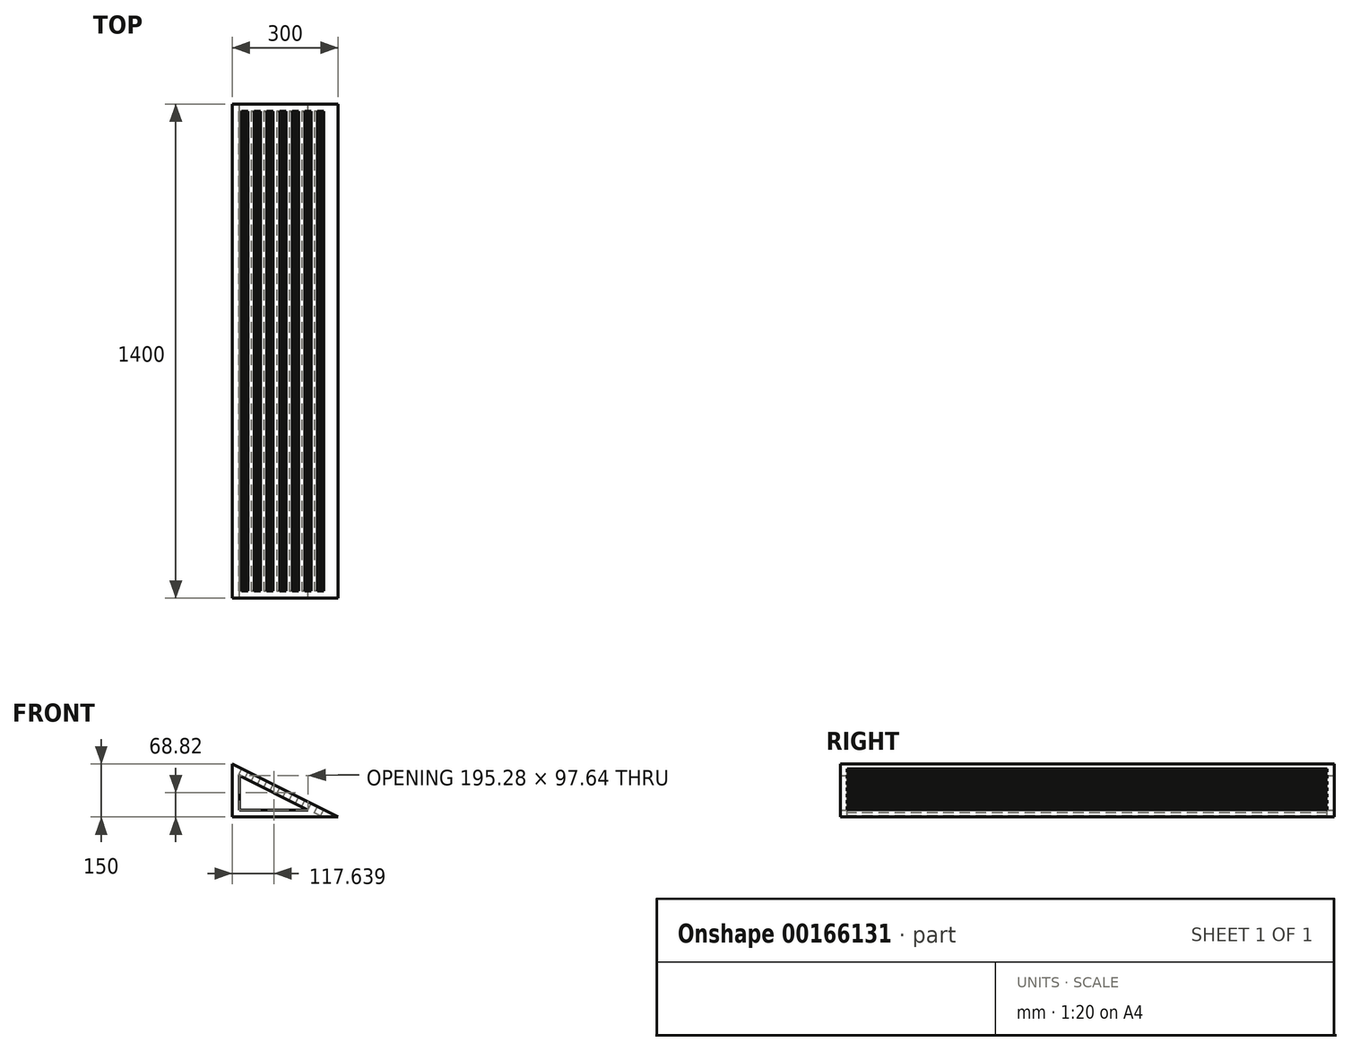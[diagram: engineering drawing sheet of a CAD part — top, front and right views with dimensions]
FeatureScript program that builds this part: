
annotation { "Feature Type Name" : "Feature", "Feature Type Description" : "" }
export const myFeature = defineFeature(function(context is Context, id is Id, definition is map)
    precondition{}
    {
        {
            var Q0;
            Q0=qCreatedBy(makeId("Front.planeOp"),FACE);
            var sketch = newSketch(context, id + "F0", { "sketchPlane" : qUnion([Q0])});
            skLineSegment(sketch, "E0", {"start": v(0, 0) * mm, "end": v(0, 150) * mm});
            skLineSegment(sketch, "E1", {"start": v(0, 150) * mm, "end": v(300, 0) * mm});
            skLineSegment(sketch, "E2", {"start": v(300, 0) * mm, "end": v(0, 0) * mm});
            skLineSegment(sketch, "E3", {"start": v(20, 20) * mm, "end": v(20, 117.64) * mm});
            skLineSegment(sketch, "E4", {"start": v(20, 117.64) * mm, "end": v(215.28, 20) * mm});
            skLineSegment(sketch, "E5", {"start": v(215.28, 20) * mm, "end": v(20, 20) * mm});
            skSolve(sketch);
        }
        {
            var Q0;
            Q0 = qSketchRegion(id + "F0", true);
            extrude(context, id + "F1", {"entities" : qUnion([Q0]), "depth" : 1400 * mm});
        }
        {
            var Q0;
            Q0=makeQuery(id+"F1.opExtrude","SWEPT_FACE",FACE,{"disambiguationData":[OSD([sQuery(id+"F0.wireOp",EDGE,"E1")])]});
            var sketch = newSketch(context, id + "F2", { "sketchPlane" : qUnion([Q0])});
            skLineSegment(sketch, "E6.bottom", {"start": v(-37.08, -1380) * mm, "end": v(-17.08, -1380) * mm});
            skLineSegment(sketch, "E6.top", {"start": v(-37.08, -20) * mm, "end": v(-17.08, -20) * mm});
            skLineSegment(sketch, "E6.left", {"start": v(-37.08, -1380) * mm, "end": v(-37.08, -20) * mm});
            skLineSegment(sketch, "E6.right", {"start": v(-17.08, -1380) * mm, "end": v(-17.08, -20) * mm});
            skLineSegment(sketch, "E7.bottom", {"start": v(2.92, -1380) * mm, "end": v(22.92, -1380) * mm});
            skLineSegment(sketch, "E7.top", {"start": v(2.92, -20) * mm, "end": v(22.92, -20) * mm});
            skLineSegment(sketch, "E7.left", {"start": v(2.92, -1380) * mm, "end": v(2.92, -20) * mm});
            skLineSegment(sketch, "E7.right", {"start": v(22.92, -1380) * mm, "end": v(22.92, -20) * mm});
            skLineSegment(sketch, "E8.bottom", {"start": v(42.92, -1380) * mm, "end": v(62.92, -1380) * mm});
            skLineSegment(sketch, "E8.top", {"start": v(42.92, -20) * mm, "end": v(62.92, -20) * mm});
            skLineSegment(sketch, "E8.left", {"start": v(42.92, -1380) * mm, "end": v(42.92, -20) * mm});
            skLineSegment(sketch, "E8.right", {"start": v(62.92, -1380) * mm, "end": v(62.92, -20) * mm});
            skLineSegment(sketch, "E9.bottom", {"start": v(82.92, -1380) * mm, "end": v(102.92, -1380) * mm});
            skLineSegment(sketch, "E9.top", {"start": v(82.92, -20) * mm, "end": v(102.92, -20) * mm});
            skLineSegment(sketch, "E9.left", {"start": v(82.92, -1380) * mm, "end": v(82.92, -20) * mm});
            skLineSegment(sketch, "E9.right", {"start": v(102.92, -1380) * mm, "end": v(102.92, -20) * mm});
            skLineSegment(sketch, "E10.bottom", {"start": v(122.92, -1380) * mm, "end": v(142.92, -1380) * mm});
            skLineSegment(sketch, "E10.top", {"start": v(122.92, -20) * mm, "end": v(142.92, -20) * mm});
            skLineSegment(sketch, "E10.left", {"start": v(122.92, -1380) * mm, "end": v(122.92, -20) * mm});
            skLineSegment(sketch, "E10.right", {"start": v(142.92, -1380) * mm, "end": v(142.92, -20) * mm});
            skLineSegment(sketch, "E11.bottom", {"start": v(162.92, -1380) * mm, "end": v(182.92, -1380) * mm});
            skLineSegment(sketch, "E11.top", {"start": v(162.92, -20) * mm, "end": v(182.92, -20) * mm});
            skLineSegment(sketch, "E11.left", {"start": v(162.92, -1380) * mm, "end": v(162.92, -20) * mm});
            skLineSegment(sketch, "E11.right", {"start": v(182.92, -1380) * mm, "end": v(182.92, -20) * mm});
            skLineSegment(sketch, "E12.bottom", {"start": v(202.92, -1380) * mm, "end": v(222.92, -1380) * mm});
            skLineSegment(sketch, "E12.top", {"start": v(202.92, -20) * mm, "end": v(222.92, -20) * mm});
            skLineSegment(sketch, "E12.left", {"start": v(202.92, -1380) * mm, "end": v(202.92, -20) * mm});
            skLineSegment(sketch, "E12.right", {"start": v(222.92, -1380) * mm, "end": v(222.92, -20) * mm});
            skSolve(sketch);
        }
        {
            var Q0;
            Q0 = qSketchRegion(id + "F2", true);
            var Q1;
            Q1=makeQuery(id+"F1.opExtrude","SWEPT_FACE",FACE,{"disambiguationData":[OSD([sQuery(id+"F0.wireOp",EDGE,"E4")])]});
            extrude(context, id + "F3", {"entities" : qUnion([Q0]), "operationType" : NewBodyOperationType.REMOVE, "endBound" : BoundingType.UP_TO_SURFACE, "oppositeDirection" : true, "endBoundEntityFace" : qUnion([Q1]), "depth" : 25 * mm});
        }
    });
